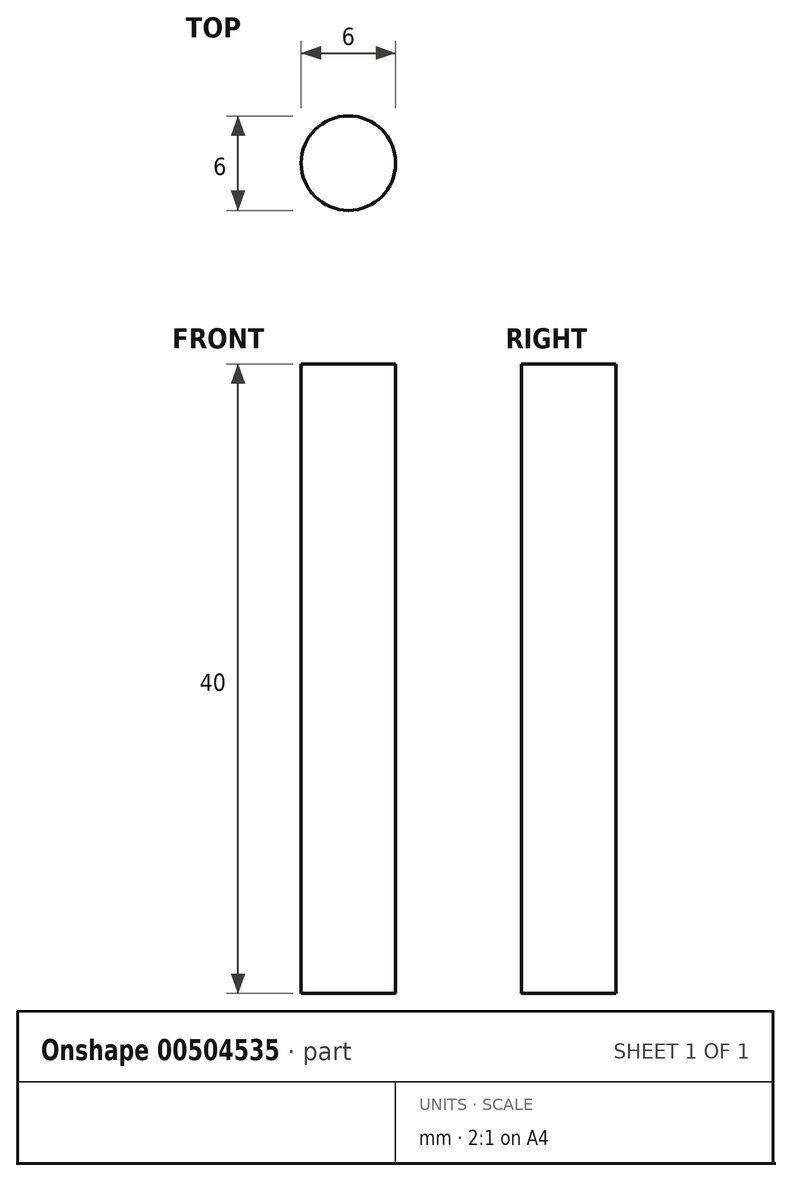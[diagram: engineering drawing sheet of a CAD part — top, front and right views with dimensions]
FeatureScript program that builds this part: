
annotation { "Feature Type Name" : "Feature", "Feature Type Description" : "" }
export const myFeature = defineFeature(function(context is Context, id is Id, definition is map)
    precondition{}
    {
        {
            var Q0;
            Q0=qCreatedBy(makeId("Top.planeOp"),FACE);
            var sketch = newSketch(context, id + "F0", { "sketchPlane" : qUnion([Q0])});
            skCircle(sketch, "E0", {"center": v(0, 0) * mm, "radius": 3 * mm});
            skSolve(sketch);
        }
        {
            var Q0;
            Q0 = qSketchRegion(id + "F0", true);
            extrude(context, id + "F1", {"entities" : qUnion([Q0]), "depth" : 40 * mm});
        }
    });
